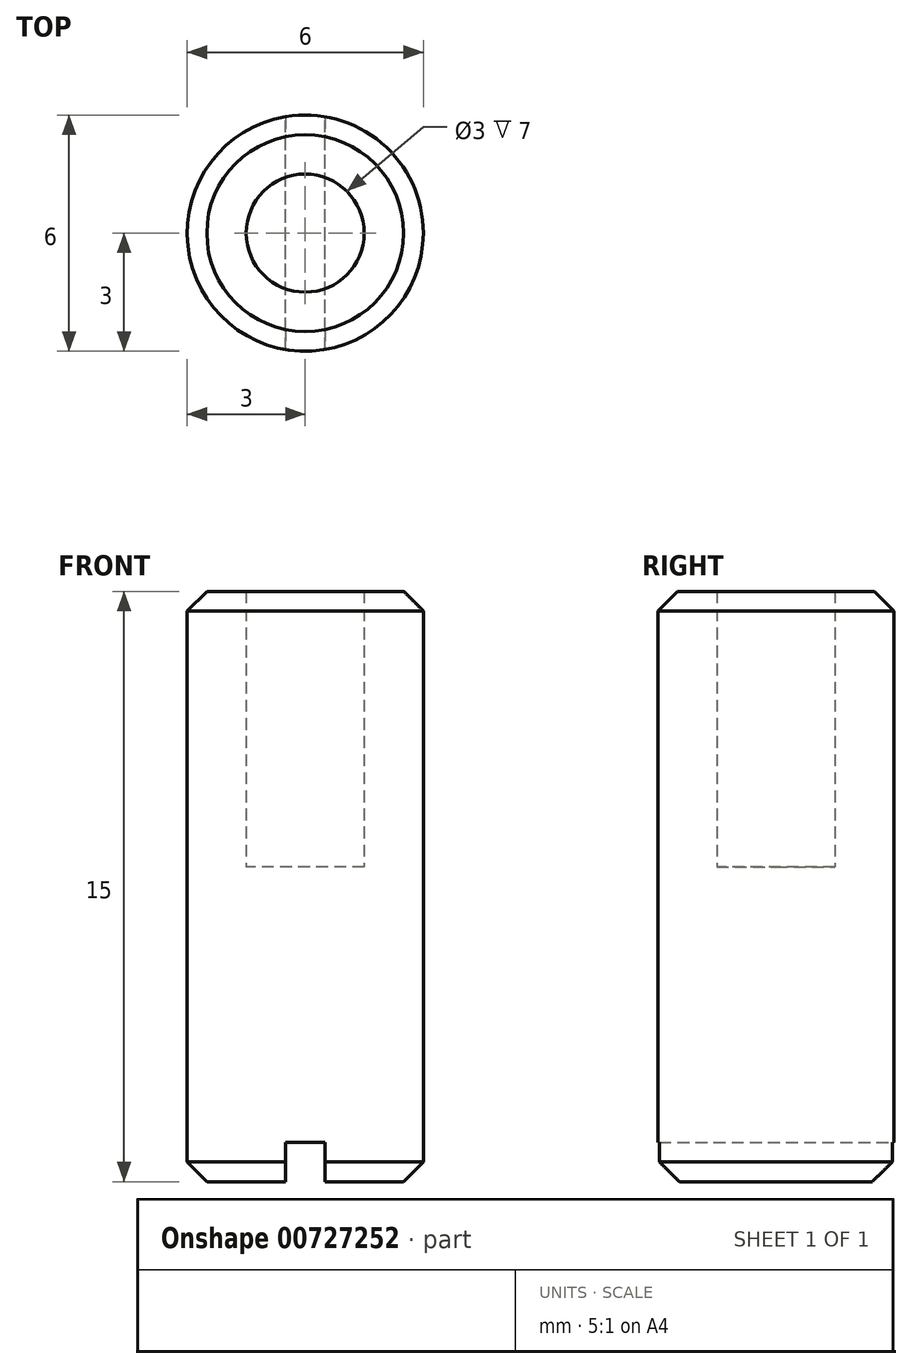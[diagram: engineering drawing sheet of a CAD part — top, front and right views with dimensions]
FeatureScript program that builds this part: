
annotation { "Feature Type Name" : "Feature", "Feature Type Description" : "" }
export const myFeature = defineFeature(function(context is Context, id is Id, definition is map)
    precondition{}
    {
        {
            var Q0;
            Q0=qCreatedBy(makeId("Top.planeOp"),FACE);
            var sketch = newSketch(context, id + "F0", { "sketchPlane" : qUnion([Q0])});
            skCircle(sketch, "E0", {"center": v(0, 0) * mm, "radius": 1.5 * mm});
            skCircle(sketch, "E1", {"center": v(0, 0) * mm, "radius": 3 * mm});
            skSolve(sketch);
        }
        {
            var Q0;
            Q0=makeQuery(id+"F0.imprint","IMPRINT",FACE,{"disambiguationData":[TD([[makeQuery(id+"F0.imprint","IMPRINT",EDGE,{"derivedFrom":sQuery(id+"F0.wireOp",EDGE,"E0")}),-1.0]])]});
            extrude(context, id + "F1", {"entities" : qUnion([Q0]), "depth" : 15 * mm, "offsetDistance" : 25 * mm});
        }
        {
            var Q0;
            Q0=makeQuery(id+"F0.imprint","IMPRINT",FACE,{"disambiguationData":[TD([[makeQuery(id+"F0.imprint","IMPRINT",EDGE,{"derivedFrom":sQuery(id+"F0.wireOp",EDGE,"E0")}),1.0]])]});
            extrude(context, id + "F2", {"entities" : qUnion([Q0]), "operationType" : NewBodyOperationType.ADD, "depth" : 8 * mm, "offsetDistance" : 25 * mm});
        }
        {
            var Q0;
            Q0=makeQuery(id+"F1.opExtrude","CAP_EDGE",EDGE,{"disambiguationData":[OSD([sQuery(id+"F0.wireOp",EDGE,"E1")])],"isStart":true});
            var Q1;
            Q1=makeQuery(id+"F1.opExtrude","CAP_EDGE",EDGE,{"disambiguationData":[OSD([sQuery(id+"F0.wireOp",EDGE,"E1")])],"isStart":false});
            chamfer(context, id + "F3", {"entities" : qUnion([Q0, Q1]), "width" : 0.5 * mm, "tangentPropagation" : true});
        }
        {
            var Q0;
            Q0=qCreatedBy(makeId("Front.planeOp"),FACE);
            var sketch = newSketch(context, id + "F4", { "sketchPlane" : qUnion([Q0])});
            skLineSegment(sketch, "E2.bottom", {"start": v(-0.5, 1) * mm, "end": v(0.5, 1) * mm});
            skLineSegment(sketch, "E2.top", {"start": v(-0.5, -1) * mm, "end": v(0.5, -1) * mm});
            skLineSegment(sketch, "E2.left", {"start": v(-0.5, 1) * mm, "end": v(-0.5, -1) * mm});
            skLineSegment(sketch, "E2.right", {"start": v(0.5, 1) * mm, "end": v(0.5, -1) * mm});
            skPoint(sketch, "E2.middle", {"position": v(0, 0) * mm});
            skSolve(sketch);
        }
        {
            var Q0;
            Q0 = qSketchRegion(id + "F4", true);
            extrude(context, id + "F5", {"entities" : qUnion([Q0]), "operationType" : NewBodyOperationType.REMOVE, "endBound" : BoundingType.SYMMETRIC, "depth" : 25 * mm, "offsetDistance" : 25 * mm});
        }
    });
